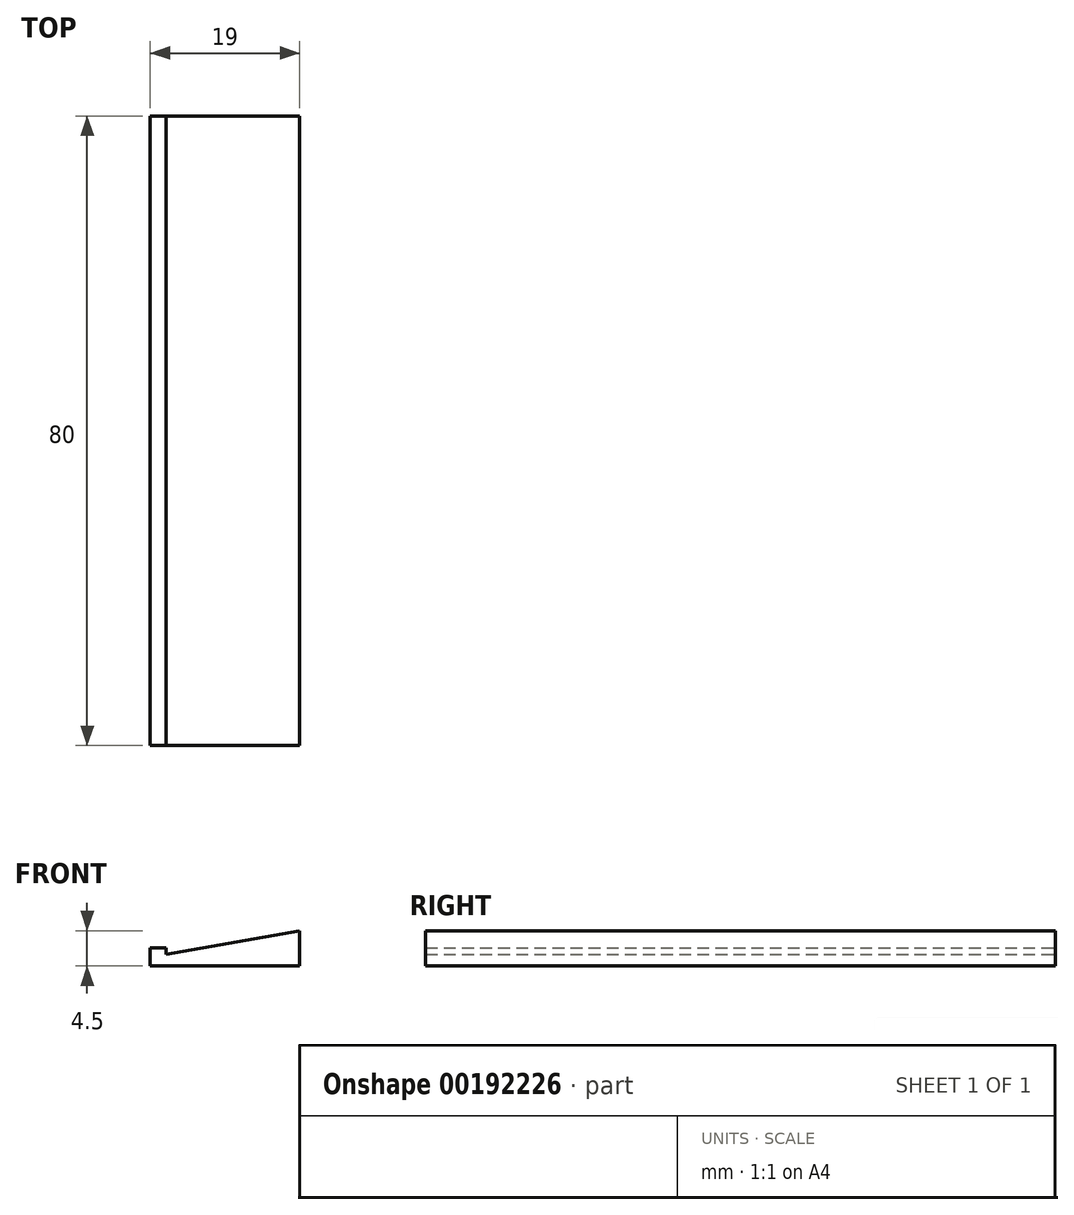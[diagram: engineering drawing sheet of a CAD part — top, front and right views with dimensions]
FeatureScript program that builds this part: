
annotation { "Feature Type Name" : "Feature", "Feature Type Description" : "" }
export const myFeature = defineFeature(function(context is Context, id is Id, definition is map)
    precondition{}
    {
        {
            var Q0;
            Q0=qCreatedBy(makeId("Front.planeOp"),FACE);
            var sketch = newSketch(context, id + "F0", { "sketchPlane" : qUnion([Q0])});
            skLineSegment(sketch, "E0", {"start": v(0, 0) * mm, "end": v(-19, 0) * mm});
            skLineSegment(sketch, "E1", {"start": v(-19, 0) * mm, "end": v(-19, 2.3) * mm});
            skLineSegment(sketch, "E2", {"start": v(-19, 2.3) * mm, "end": v(-17.01, 2.3) * mm});
            skLineSegment(sketch, "E3", {"start": v(-17.01, 2.3) * mm, "end": v(-17.01, 1.5) * mm});
            skLineSegment(sketch, "E4", {"start": v(-17.01, 1.5) * mm, "end": v(0, 4.5) * mm});
            skLineSegment(sketch, "E5", {"start": v(0, 4.5) * mm, "end": v(0, 0) * mm});
            skSolve(sketch);
        }
        {
            var Q0;
            Q0=makeQuery(id+"F0.imprint","IMPRINT",FACE,{"disambiguationData":[TD([[makeQuery(id+"F0.imprint","IMPRINT",EDGE,{"derivedFrom":sQuery(id+"F0.wireOp",EDGE,"E0")}),-1.0]])]});
            extrude(context, id + "F1", {"entities" : qUnion([Q0]), "depth" : 80 * mm});
        }
    });
